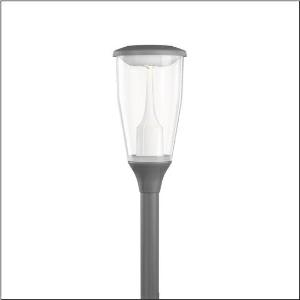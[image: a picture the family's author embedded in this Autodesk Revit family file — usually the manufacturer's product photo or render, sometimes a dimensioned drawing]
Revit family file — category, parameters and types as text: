
# Revit family: dl_11_iq___st1_2a_5xa5565mf14hp00022_149f
name_source: partatom
category: Lighting Fixtures
units: mm (PartAtom-declared; Revit-internal decimal feet)

## family parameters
Cut with Voids When Loaded = No
Host = Face
Light Source = No
Part Type = Normal
Room Calculation Point = No
Round Connector Dimension = Use Diameter
Shared = No

## types (1)
- --- (1 x LED, 4340 lm, 33.6 W, 2700K)
    Apparent Load = 34 VA
    CIE Flux Codes = 33 63 91 94 100
    Color Rendering = 70
    Color Temperature = 2700K
    Default Elevation = 1800 mm
    Description = DL 11 iQ, mast luminaire, Module 540 iQ-SR, primary light control with 3 zone facetted reflector, of plastic, silver coated, highly specular, structured, primary optical cover: cover, of PMMA, transparent, light distribution: ST1.2a, light emission: direct distribution, primary light characteristic: asymmetric, installation type: post-top, LED, High Power LED, light colour: 727, colour temperature: 2700K, control: Street-Remote, Auto-Match, Temp-Guard, Lumen-Switch, Night-Set, Smart-Wire, Light-Fading, Desk-Remote (wireless, voltage-free reading and setting of iQ features in the workshop via application-optimized NFC function/RFID function), optimised constant luminous flux control (CLO 2.0), mains connection: 220..240V, AC, 50/60Hz, connection cable pre-assembled, cable length: 5,5m, start of lifetime: 34W, end of service life: 36W, luminaire housing, upper part, of diecast aluminium, coated, Siteco® metallic grey (DB 702S), spigot size: 60mm (post-top), post-top mast mounting element, of diecast aluminium, coated, Siteco® metallic grey (DB 702S), Module 540 iQ-SR, traffic white (RAL 9016), equipment: Power, protection rating (complete): IP66, insulation class (complete): insulation class II (safety insulation), certification: CE, ENEC, ENEC+, VDE, packaging unit: 1 piece

Light Distribution: ST1.2a
    Height = 665 mm
    Lamp = 1 x LED
    Lamp Light Flux = 4340 lm
    Lamp Power = 33.6 W
    Lamp count = 1
    Length = 334 mm
    Luminous efficacy = 129 lm/W
    Manufacturer = Siteco
    ModVariant = No
    Model = 5XA5565MF14HP00022
    Number of Poles = 1
    OnlyDefault = Yes
    Power Factor = 1
    Product Name = DL 11 iQ | ST1.2a
    Product group = mast luminaire | pylon top
    ProductGroupID = 6100
    Protection Class = Protection class II
    Protection Degree = IP 66
    RLX_Detail_Level = 1
    RLX_Emergency_Light_Flux = 0 lm
    RLX_Emergency_Type = 0
    RLX_Emergency_Type_DB = No
    RlxData = <blob elided: 155837 chars, md5=c2bd2628>
    Socket = socket
    Standby Power = 0 W
    System Light Flux = 4340 lm
    System Power = 34 W
    Type Comments = factory setting: luminous flux: 100 % | dim-lin: 254 | 695 mA
    Type Image = l_1258354.jpg
    URL = http://relux.com
    VarID = @adj_019997
    Voltage = 0 V
    Weight = 0.00 kg
    Width = 0 mm  [stored 0 ft]

note: [stored X ft] marks values corroborated as IEEE doubles in the binary element streams (Revit-internal decimal feet)

## geometry (parser evidence)
native form markers: Blend x4, Sweep x10
no freeform markers — native parametric forms only
